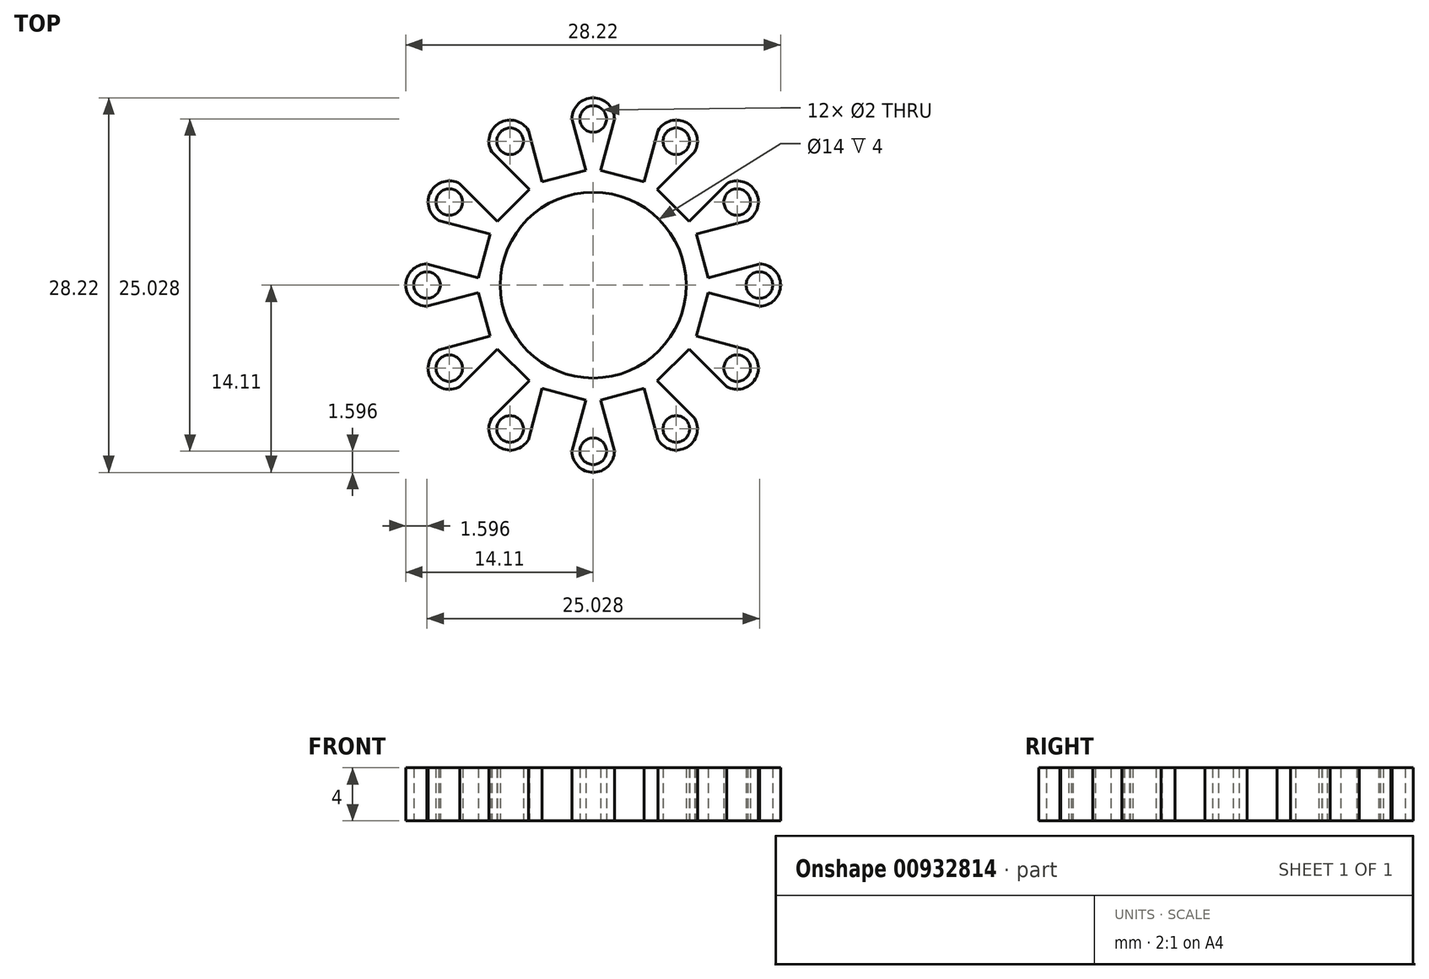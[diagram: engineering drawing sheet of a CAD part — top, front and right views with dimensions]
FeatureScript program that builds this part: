
annotation { "Feature Type Name" : "Feature", "Feature Type Description" : "" }
export const myFeature = defineFeature(function(context is Context, id is Id, definition is map)
    precondition{}
    {
        {
            var Q0;
            Q0=qCreatedBy(makeId("Top.planeOp"),FACE);
            var sketch = newSketch(context, id + "F0", { "sketchPlane" : qUnion([Q0])});
            skArc(sketch, "E0", {"start": v(8.21, 2.2) * mm, "mid": v(8.5, 0) * mm, "end": v(8.21, -2.2) * mm, "construction": true});
            skLineSegment(sketch, "E1", {"start": v(0, 0) * mm, "end": v(6.76, 1.81) * mm, "construction": true});
            skLineSegment(sketch, "E2", {"start": v(0, 0) * mm, "end": v(6.76, -1.81) * mm});
            skLineSegment(sketch, "E3", {"start": v(8.21, 2.2) * mm, "end": v(8.65, 0.56) * mm});
            skLineSegment(sketch, "E4.MirrorCS", {"start": v(8.21, -2.2) * mm, "end": v(8.65, -0.56) * mm});
            skArc(sketch, "E5", {"start": v(6.76, 1.81) * mm, "mid": v(7, 0) * mm, "end": v(6.76, -1.81) * mm});
            skLineSegment(sketch, "E6", {"start": v(6.76, 1.81) * mm, "end": v(8.21, 2.2) * mm});
            skLineSegment(sketch, "E7", {"start": v(6.76, -1.81) * mm, "end": v(8.21, -2.2) * mm});
            skLineSegment(sketch, "E8", {"start": v(8.65, 0.56) * mm, "end": v(12.51, 1.6) * mm});
            skArc(sketch, "E9", {"start": v(12.51, 1.6) * mm, "mid": v(13.64, 1.13) * mm, "end": v(14.1, 0) * mm});
            skArc(sketch, "E10.MirrorCS", {"start": v(12.51, -1.6) * mm, "mid": v(13.64, -1.13) * mm, "end": v(14.1, 0) * mm});
            skLineSegment(sketch, "E11.MirrorCS", {"start": v(8.65, -0.56) * mm, "end": v(12.51, -1.6) * mm});
            skCircle(sketch, "E12", {"center": v(12.51, 0) * mm, "radius": 1 * mm});
            skSolve(sketch);
        }
        {
            var Q0;
            Q0=makeQuery(id+"F0.imprint","IMPRINT",FACE,{"disambiguationData":[TD([[makeQuery(id+"F0.imprint","IMPRINT",EDGE,{"derivedFrom":sQuery(id+"F0.wireOp",EDGE,"E3")}),-1.0]])]});
            extrude(context, id + "F1", {"entities" : qUnion([Q0]), "depth" : 4 * mm, "offsetDistance" : 25 * mm});
        }
        {
            var Q0;
            Q0=qCreatedBy(makeId("Front.planeOp"),FACE);
            var sketch = newSketch(context, id + "F2", { "sketchPlane" : qUnion([Q0])});
            skLineSegment(sketch, "E13", {"start": v(0, 15.78) * mm, "end": v(0, -26.73) * mm, "construction": true});
            skSolve(sketch);
        }
        {
            var Q0;
            Q0=makeQuery(id+"F1.opExtrude","SWEPT_BODY",BODY,{"disambiguationData":[OSD([sQuery(id+"F0.wireOp",EDGE,"E3"),sQuery(id+"F0.wireOp",EDGE,"E4.MirrorCS"),sQuery(id+"F0.wireOp",EDGE,"E5"),sQuery(id+"F0.wireOp",EDGE,"E6"),sQuery(id+"F0.wireOp",EDGE,"E7"),sQuery(id+"F0.wireOp",EDGE,"E8"),sQuery(id+"F0.wireOp",EDGE,"E9"),sQuery(id+"F0.wireOp",EDGE,"E10.MirrorCS"),sQuery(id+"F0.wireOp",EDGE,"E11.MirrorCS"),sQuery(id+"F0.wireOp",EDGE,"E12")])]});
            var Q1;
            Q1=sQuery(id+"F2.wireOp",EDGE,"E13");
            circularPattern(context, id + "F3", {"operationType" : NewBodyOperationType.ADD, "entities" : qUnion([Q0]), "axis" : qUnion([Q1]), "angle" : 360 * degree, "instanceCount" : 12, "equalSpace" : true});
        }
    });
